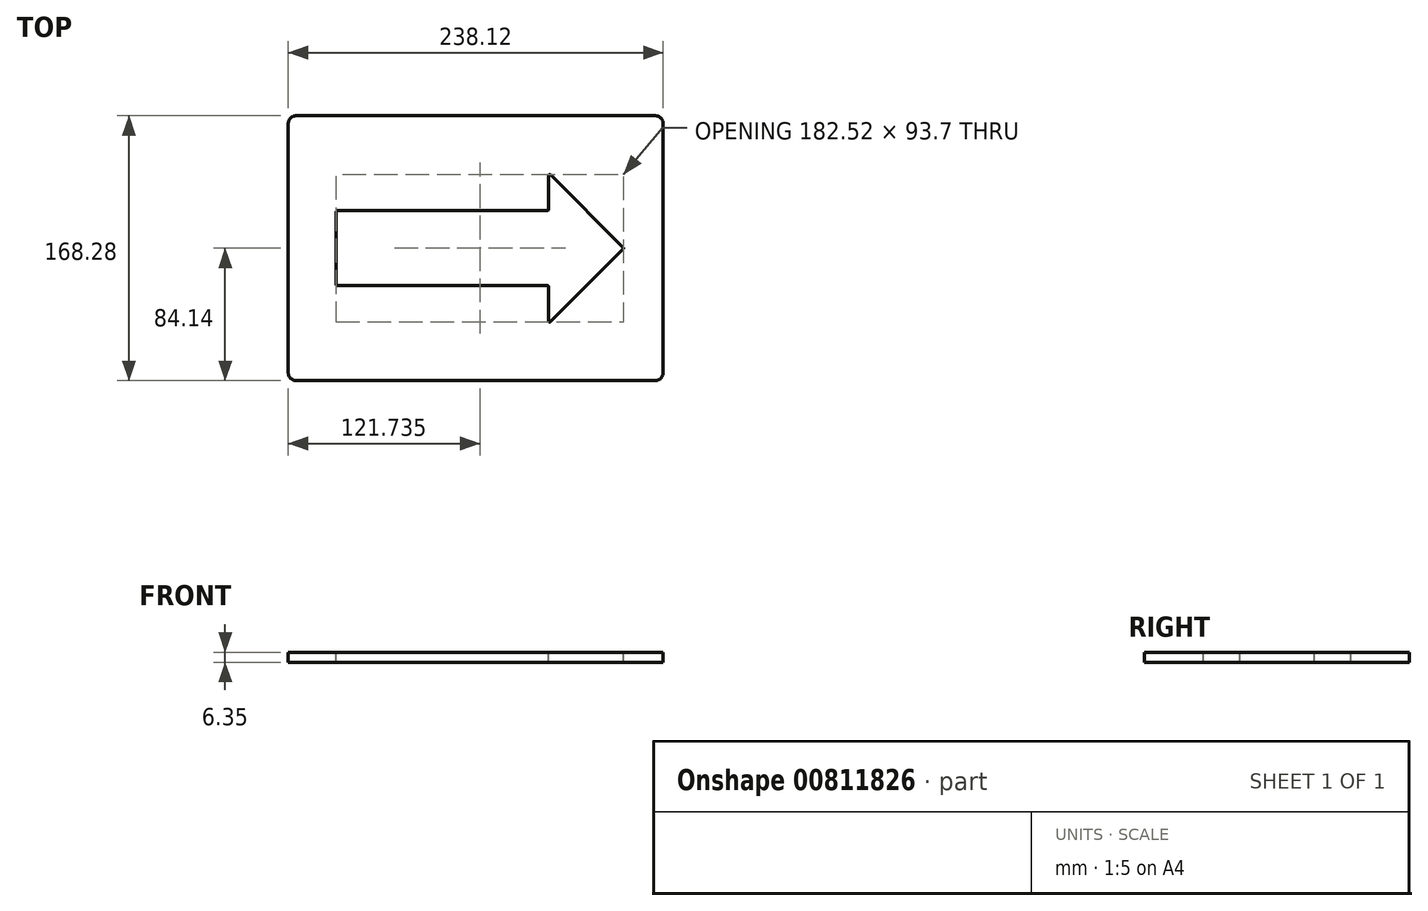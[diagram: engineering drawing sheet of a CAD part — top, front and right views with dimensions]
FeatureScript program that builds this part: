
annotation { "Feature Type Name" : "Feature", "Feature Type Description" : "" }
export const myFeature = defineFeature(function(context is Context, id is Id, definition is map)
    precondition{}
    {
        {
            var Q0;
            Q0=qCreatedBy(makeId("Top.planeOp"),FACE);
            var sketch = newSketch(context, id + "F0", { "sketchPlane" : qUnion([Q0])});
            skLineSegment(sketch, "E0.bottom", {"start": v(-113.98, 84.14) * mm, "end": v(113.98, 84.14) * mm});
            skLineSegment(sketch, "E0.top", {"start": v(-113.98, -84.14) * mm, "end": v(113.98, -84.14) * mm});
            skLineSegment(sketch, "E0.left", {"start": v(-119.06, 79.06) * mm, "end": v(-119.06, -79.06) * mm});
            skLineSegment(sketch, "E0.right", {"start": v(119.06, 79.06) * mm, "end": v(119.06, -79.06) * mm});
            skPoint(sketch, "E0.middle", {"position": v(0, 0) * mm});
            skPoint(sketch, "E1.visualSharp", {"position": v(-119.06, 84.14) * mm});
            skArc(sketch, "E1.filletArc", {"start": v(-113.98, 84.14) * mm, "mid": v(-117.57, 82.65) * mm, "end": v(-119.06, 79.06) * mm});
            skPoint(sketch, "E2.visualSharp", {"position": v(-119.06, -84.14) * mm});
            skArc(sketch, "E2.filletArc", {"start": v(-119.06, -79.06) * mm, "mid": v(-117.57, -82.65) * mm, "end": v(-113.98, -84.14) * mm});
            skPoint(sketch, "E3.visualSharp", {"position": v(119.06, -84.14) * mm});
            skArc(sketch, "E3.filletArc", {"start": v(113.98, -84.14) * mm, "mid": v(117.57, -82.65) * mm, "end": v(119.06, -79.06) * mm});
            skPoint(sketch, "E4.visualSharp", {"position": v(119.06, 84.14) * mm});
            skArc(sketch, "E4.filletArc", {"start": v(119.06, 79.06) * mm, "mid": v(117.57, 82.65) * mm, "end": v(113.98, 84.14) * mm});
            skSolve(sketch);
        }
        {
            var Q0;
            Q0 = qSketchRegion(id + "F0", true);
            extrude(context, id + "F1", {"entities" : qUnion([Q0]), "depth" : 6.35 * mm, "offsetDistance" : 25.4 * mm});
        }
        {
            var Q0;
            Q0=makeQuery(id+"F1.opExtrude","CAP_FACE",FACE,{"disambiguationData":[OSD([sQuery(id+"F0.wireOp",EDGE,"E0.bottom"),sQuery(id+"F0.wireOp",EDGE,"E0.top"),sQuery(id+"F0.wireOp",EDGE,"E0.left"),sQuery(id+"F0.wireOp",EDGE,"E0.right"),sQuery(id+"F0.wireOp",EDGE,"E1.filletArc"),sQuery(id+"F0.wireOp",EDGE,"E2.filletArc"),sQuery(id+"F0.wireOp",EDGE,"E3.filletArc"),sQuery(id+"F0.wireOp",EDGE,"E4.filletArc")])],"isStart":false});
            var sketch = newSketch(context, id + "F2", { "sketchPlane" : qUnion([Q0])});
            skLineSegment(sketch, "E5", {"start": v(-87.31, 0) * mm, "end": v(-87.31, 22.48) * mm});
            skLineSegment(sketch, "E6", {"start": v(-87.31, 22.48) * mm, "end": v(47.56, 22.48) * mm});
            skLineSegment(sketch, "E7", {"start": v(47.56, 22.48) * mm, "end": v(47.56, 44.9) * mm});
            skLineSegment(sketch, "E8", {"start": v(47.56, 44.9) * mm, "end": v(92.46, 0) * mm});
            skLineSegment(sketch, "E9.MirrorCS", {"start": v(-87.31, -22.48) * mm, "end": v(47.56, -22.48) * mm});
            skLineSegment(sketch, "E10.MirrorCS", {"start": v(47.56, -22.48) * mm, "end": v(47.56, -44.9) * mm});
            skLineSegment(sketch, "E11.MirrorCS", {"start": v(47.56, -44.9) * mm, "end": v(92.46, 0) * mm});
            skLineSegment(sketch, "E12.MirrorCS", {"start": v(-87.31, 0) * mm, "end": v(-87.31, -22.48) * mm});
            skSolve(sketch);
        }
        {
            var Q0;
            Q0 = qSketchRegion(id + "F2", true);
            extrude(context, id + "F3", {"entities" : qUnion([Q0]), "operationType" : NewBodyOperationType.REMOVE, "endBound" : BoundingType.THROUGH_ALL, "oppositeDirection" : true, "depth" : 25.4 * mm, "offsetDistance" : 25.4 * mm});
        }
        {
            var Q0;
            Q0=makeQuery(id+"F1.opExtrude","CAP_FACE",FACE,{"disambiguationData":[OSD([sQuery(id+"F0.wireOp",EDGE,"E0.bottom"),sQuery(id+"F0.wireOp",EDGE,"E0.top"),sQuery(id+"F0.wireOp",EDGE,"E0.left"),sQuery(id+"F0.wireOp",EDGE,"E0.right"),sQuery(id+"F0.wireOp",EDGE,"E1.filletArc"),sQuery(id+"F0.wireOp",EDGE,"E2.filletArc"),sQuery(id+"F0.wireOp",EDGE,"E3.filletArc"),sQuery(id+"F0.wireOp",EDGE,"E4.filletArc")])],"isStart":false});
            var sketch = newSketch(context, id + "F4", { "sketchPlane" : qUnion([Q0])});
            skLineSegment(sketch, "E13.0", {"start": v(-88.58, -22.96) * mm, "end": v(-88.58, 22.96) * mm});
            skLineSegment(sketch, "E13.1", {"start": v(-87.8, -23.75) * mm, "end": v(45.5, -23.75) * mm});
            skLineSegment(sketch, "E13.2", {"start": v(46.3, 24.54) * mm, "end": v(46.3, 46.07) * mm});
            skLineSegment(sketch, "E13.3", {"start": v(47.64, 46.62) * mm, "end": v(93.7, 0.56) * mm});
            skLineSegment(sketch, "E13.4", {"start": v(47.64, -46.62) * mm, "end": v(93.7, -0.56) * mm});
            skLineSegment(sketch, "E13.5", {"start": v(-87.8, 23.75) * mm, "end": v(45.5, 23.75) * mm});
            skLineSegment(sketch, "E13.6", {"start": v(46.3, -24.54) * mm, "end": v(46.3, -46.07) * mm});
            skPoint(sketch, "E14.visualSharp", {"position": v(-88.58, -23.75) * mm});
            skArc(sketch, "E14.filletArc", {"start": v(-88.58, -22.96) * mm, "mid": v(-88.35, -23.52) * mm, "end": v(-87.8, -23.75) * mm});
            skPoint(sketch, "E15.visualSharp", {"position": v(-88.58, 23.75) * mm});
            skArc(sketch, "E15.filletArc", {"start": v(-87.8, 23.75) * mm, "mid": v(-88.35, 23.52) * mm, "end": v(-88.58, 22.96) * mm});
            skPoint(sketch, "E16.visualSharp", {"position": v(46.3, 23.75) * mm});
            skArc(sketch, "E16.filletArc", {"start": v(45.5, 23.75) * mm, "mid": v(46.06, 23.98) * mm, "end": v(46.3, 24.54) * mm});
            skPoint(sketch, "E17.visualSharp", {"position": v(46.3, 47.97) * mm});
            skArc(sketch, "E17.filletArc", {"start": v(47.64, 46.62) * mm, "mid": v(46.78, 46.8) * mm, "end": v(46.3, 46.07) * mm});
            skPoint(sketch, "E18.visualSharp", {"position": v(94.26, 0) * mm});
            skArc(sketch, "E18.filletArc", {"start": v(93.7, -0.56) * mm, "mid": v(93.93, 0) * mm, "end": v(93.7, 0.56) * mm});
            skPoint(sketch, "E19.visualSharp", {"position": v(46.3, -47.97) * mm});
            skArc(sketch, "E19.filletArc", {"start": v(46.3, -46.07) * mm, "mid": v(46.78, -46.8) * mm, "end": v(47.64, -46.62) * mm});
            skPoint(sketch, "E20.visualSharp", {"position": v(46.3, -23.75) * mm});
            skArc(sketch, "E20.filletArc", {"start": v(46.3, -24.54) * mm, "mid": v(46.06, -23.98) * mm, "end": v(45.5, -23.75) * mm});
            skSolve(sketch);
        }
        {
            var Q0;
            Q0 = qSketchRegion(id + "F4", true);
            extrude(context, id + "F5", {"entities" : qUnion([Q0]), "operationType" : NewBodyOperationType.REMOVE, "endBound" : BoundingType.THROUGH_ALL, "oppositeDirection" : true, "depth" : 25.4 * mm, "offsetDistance" : 25.4 * mm});
        }
    });
